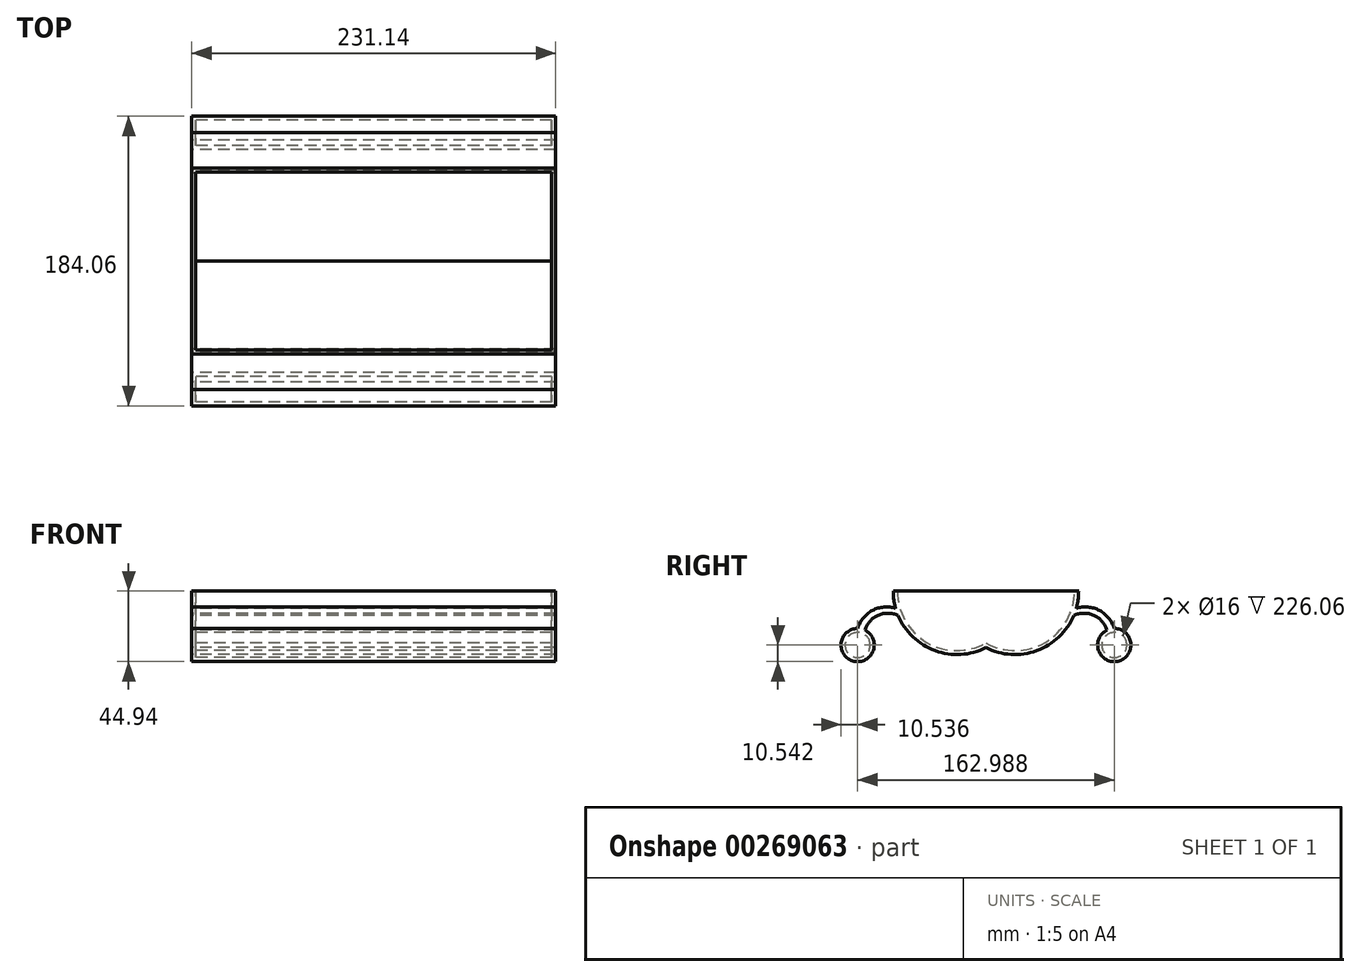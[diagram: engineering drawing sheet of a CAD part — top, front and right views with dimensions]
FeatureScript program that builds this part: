
annotation { "Feature Type Name" : "Feature", "Feature Type Description" : "" }
export const myFeature = defineFeature(function(context is Context, id is Id, definition is map)
    precondition{}
    {
        {
            var Q0;
            Q0=qCreatedBy(makeId("Right.planeOp"),FACE);
            var sketch = newSketch(context, id + "F0", { "sketchPlane" : qUnion([Q0])});
            skLineSegment(sketch, "E0", {"start": v(0, 0) * mm, "end": v(58.9, 0) * mm});
            skLineSegment(sketch, "E1", {"start": v(0, 0) * mm, "end": v(0, -35.99) * mm});
            skArc(sketch, "E2", {"start": v(0, -35.99) * mm, "mid": v(39.53, -34.48) * mm, "end": v(58.9, 0) * mm});
            skCircle(sketch, "E3", {"center": v(81.5, -34.4) * mm, "radius": 10.54 * mm});
            skLineSegment(sketch, "E4", {"start": v(81.5, -34.4) * mm, "end": v(76.83, -34.4) * mm});
            skArc(sketch, "E5", {"start": v(81.5, -34.4) * mm, "mid": v(76.4, -15.51) * mm, "end": v(57.33, -11.1) * mm});
            skArc(sketch, "E6", {"start": v(76.83, -34.4) * mm, "mid": v(72.48, -18.05) * mm, "end": v(55.74, -15.61) * mm});
            skSolve(sketch);
        }
        {
            var Q0;
            {var subQ1=sQuery(id+"F0.wireOp",EDGE,"E0");Q0=makeQuery(id+"F0.imprint","IMPRINT",FACE,{"disambiguationData":[TD([[makeQuery(id+"F0.imprint","IMPRINT",EDGE,{"derivedFrom":subQ1}),-1.0]])]});}
            var Q1;
            {var subQ0=sQuery(id+"F0.wireOp",EDGE,"5mKPN1bV-Q3SY-LzZp-XUF1-PMudFkY3Y8MB");var subQ1=sQuery(id+"F0.wireOp",EDGE,"E2");var subQ2=makeQuery(id+"F0.imprint","INTERSECT",VERTEX,{"derivedFrom":[subQ1,subQ0]});Q1=makeQuery(id+"F0.imprint","IMPRINT",FACE,{"disambiguationData":[TD([[makeQuery(id+"F0.imprint","IMPRINT",EDGE,{"disambiguationData":[TD([[subQ2,-1.0]])],"derivedFrom":subQ1}),1.0]])]});}
            var Q2;
            {var subQ5=sQuery(id+"F0.wireOp",EDGE,"E4");Q2=makeQuery(id+"F0.imprint","IMPRINT",FACE,{"disambiguationData":[TD([[makeQuery(id+"F0.imprint","IMPRINT",EDGE,{"derivedFrom":subQ5}),-1.0]])]});}
            var Q3;
            {var subQ5=sQuery(id+"F0.wireOp",EDGE,"E4");Q3=makeQuery(id+"F0.imprint","IMPRINT",FACE,{"disambiguationData":[TD([[makeQuery(id+"F0.imprint","IMPRINT",EDGE,{"derivedFrom":subQ5}),1.0]])]});}
            var Q4;
            {var subQ0=sQuery(id+"F0.wireOp",EDGE,"5mKPN1bV-Q3SY-LzZp-XUF1-PMudFkY3Y8MB");var subQ1=sQuery(id+"F0.wireOp",EDGE,"E2");var subQ2=makeQuery(id+"F0.imprint","INTERSECT",VERTEX,{"derivedFrom":[subQ1,subQ0]});Q4=makeQuery(id+"F0.imprint","IMPRINT",FACE,{"disambiguationData":[TD([[makeQuery(id+"F0.imprint","IMPRINT",EDGE,{"disambiguationData":[TD([[subQ2,-1.0]])],"derivedFrom":subQ1}),-1.0]])]});}
            extrude(context, id + "F1", {"entities" : qUnion([Q0, Q1, Q2, Q3, Q4]), "endBound" : BoundingType.SYMMETRIC, "depth" : 231.14 * mm});
        }
        {
            var Q0;
            Q0=makeQuery(id+"F1.opExtrude","SWEPT_BODY",BODY,{"disambiguationData":[OSD([sQuery(id+"F0.wireOp",EDGE,"E0"),sQuery(id+"F0.wireOp",EDGE,"E1"),sQuery(id+"F0.wireOp",EDGE,"E2"),sQuery(id+"F0.wireOp",EDGE,"E3"),sQuery(id+"F0.wireOp",EDGE,"7VaU7yDV-pxS2-c2U8-SAn2-95HNhZaLWVVz"),sQuery(id+"F0.wireOp",EDGE,"5mKPN1bV-Q3SY-LzZp-XUF1-PMudFkY3Y8MB")])]});
            var Q1;
            Q1=qCreatedBy(makeId("Front.planeOp"),FACE);
            mirror(context, id + "F2", {"operationType" : NewBodyOperationType.ADD, "entities" : qUnion([Q0]), "mirrorPlane" : qUnion([Q1])});
        }
        {
            var Q0;
            {var subQ0=makeQuery(id+"F1.opExtrude","SWEPT_FACE",FACE,{"disambiguationData":[OSD([sQuery(id+"F0.wireOp",EDGE,"E0")])]});Q0=makeQuery(id+"F2.boolean.opBoolean","MERGE",FACE,{"derivedFrom":[subQ0,makeQuery(id+"F2.opPattern","COPY",FACE,{"derivedFrom":subQ0,"instanceName":"1"})]});}
            shell(context, id + "F3", {"entities" : qUnion([Q0]), "thickness" : 2.54 * mm});
        }
    });
